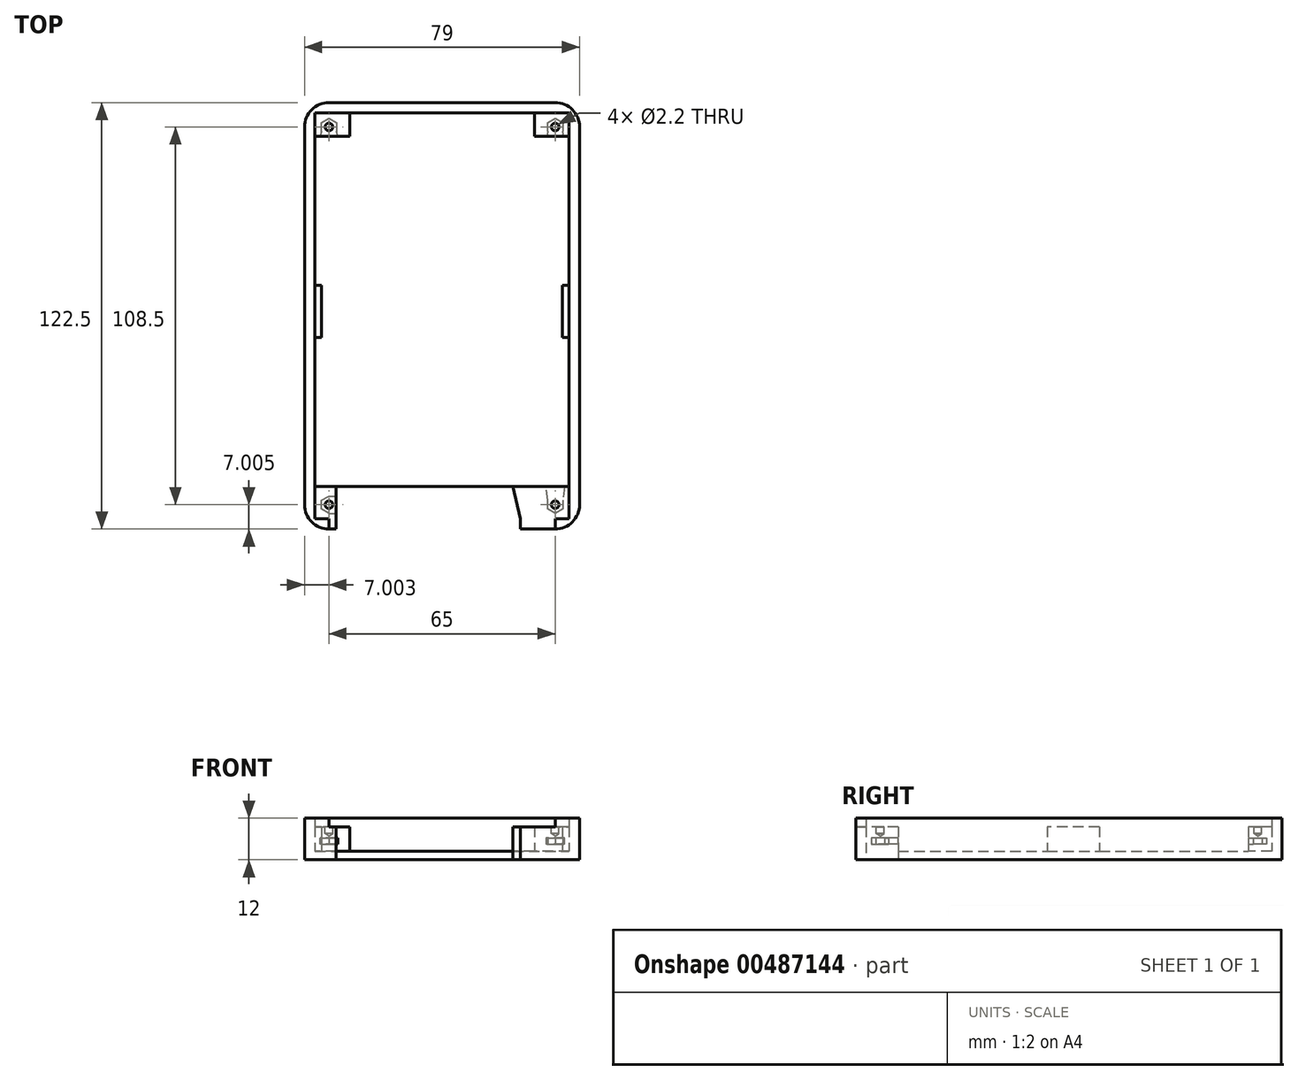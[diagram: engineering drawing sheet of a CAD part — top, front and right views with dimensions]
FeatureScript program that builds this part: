
annotation { "Feature Type Name" : "Feature", "Feature Type Description" : "" }
export const myFeature = defineFeature(function(context is Context, id is Id, definition is map)
    precondition{}
    {
        {
            var Q0;
            Q0=qCreatedBy(makeId("Top.planeOp"),FACE);
            var sketch = newSketch(context, id + "F0", { "sketchPlane" : qUnion([Q0])});
            skLineSegment(sketch, "E0.bottom", {"start": v(-32.56, 61.92) * mm, "end": v(32.44, 61.92) * mm});
            skLineSegment(sketch, "E0.top", {"start": v(-32.56, -60.58) * mm, "end": v(32.44, -60.58) * mm});
            skLineSegment(sketch, "E0.left", {"start": v(-39.56, 54.92) * mm, "end": v(-39.56, -53.58) * mm});
            skLineSegment(sketch, "E0.right", {"start": v(39.44, 54.92) * mm, "end": v(39.44, -53.58) * mm});
            skPoint(sketch, "E1.visualSharp", {"position": v(-39.56, 61.92) * mm});
            skArc(sketch, "E1.filletArc", {"start": v(-32.56, 61.92) * mm, "mid": v(-37.5, 59.87) * mm, "end": v(-39.56, 54.92) * mm});
            skPoint(sketch, "E2.visualSharp", {"position": v(39.44, 61.92) * mm});
            skArc(sketch, "E2.filletArc", {"start": v(39.44, 54.92) * mm, "mid": v(37.4, 59.87) * mm, "end": v(32.44, 61.92) * mm});
            skPoint(sketch, "E3.visualSharp", {"position": v(-39.56, -60.58) * mm});
            skArc(sketch, "E3.filletArc", {"start": v(-39.56, -53.58) * mm, "mid": v(-37.5, -58.53) * mm, "end": v(-32.56, -60.58) * mm});
            skPoint(sketch, "E4.visualSharp", {"position": v(39.44, -60.58) * mm});
            skArc(sketch, "E4.filletArc", {"start": v(32.44, -60.58) * mm, "mid": v(37.4, -58.53) * mm, "end": v(39.44, -53.58) * mm});
            skLineSegment(sketch, "E5.bottom", {"start": v(-32.56, 58.92) * mm, "end": v(32.44, 58.92) * mm});
            skLineSegment(sketch, "E5.top", {"start": v(-32.56, -57.58) * mm, "end": v(32.44, -57.58) * mm});
            skLineSegment(sketch, "E5.left", {"start": v(-36.56, 54.92) * mm, "end": v(-36.56, -53.58) * mm});
            skLineSegment(sketch, "E5.right", {"start": v(36.44, 54.92) * mm, "end": v(36.44, -53.58) * mm});
            skPoint(sketch, "E6.visualSharp", {"position": v(-36.56, 58.92) * mm});
            skArc(sketch, "E6.filletArc", {"start": v(-32.56, 58.92) * mm, "mid": v(-35.39, 57.75) * mm, "end": v(-36.56, 54.92) * mm});
            skPoint(sketch, "E7.visualSharp", {"position": v(36.44, 58.92) * mm});
            skArc(sketch, "E7.filletArc", {"start": v(36.44, 54.92) * mm, "mid": v(35.27, 57.75) * mm, "end": v(32.44, 58.92) * mm});
            skPoint(sketch, "E8.visualSharp", {"position": v(-36.56, -57.58) * mm});
            skArc(sketch, "E8.filletArc", {"start": v(-36.56, -53.58) * mm, "mid": v(-35.39, -56.4) * mm, "end": v(-32.56, -57.58) * mm});
            skPoint(sketch, "E9.visualSharp", {"position": v(36.44, -57.58) * mm});
            skArc(sketch, "E9.filletArc", {"start": v(32.44, -57.58) * mm, "mid": v(35.27, -56.4) * mm, "end": v(36.44, -53.58) * mm});
            skSolve(sketch);
        }
        {
            var Q0;
            Q0=qCreatedBy(makeId("Top.planeOp"),FACE);
            var sketch = newSketch(context, id + "F1", { "sketchPlane" : qUnion([Q0])});
            skLineSegment(sketch, "E10.bottom", {"start": v(-34.66, 51.92) * mm, "end": v(34.54, 51.92) * mm});
            skLineSegment(sketch, "E10.top", {"start": v(-34.66, -48.08) * mm, "end": v(34.54, -48.08) * mm});
            skLineSegment(sketch, "E10.left", {"start": v(-34.66, 51.92) * mm, "end": v(-34.66, -48.08) * mm});
            skLineSegment(sketch, "E10.right", {"start": v(34.54, 51.92) * mm, "end": v(34.54, -48.08) * mm});
            skSolve(sketch);
        }
        {
            var Q0;
            Q0=qCreatedBy(makeId("Top.planeOp"),FACE);
            var sketch = newSketch(context, id + "F2", { "sketchPlane" : qUnion([Q0])});
            skLineSegment(sketch, "E11.bottom", {"start": v(-34.66, 9.42) * mm, "end": v(-36.56, 9.42) * mm});
            skLineSegment(sketch, "E11.top", {"start": v(-34.66, -5.58) * mm, "end": v(-36.56, -5.58) * mm});
            skLineSegment(sketch, "E11.left", {"start": v(-34.66, 9.42) * mm, "end": v(-34.66, -5.58) * mm});
            skLineSegment(sketch, "E11.right", {"start": v(-36.56, 9.42) * mm, "end": v(-36.56, -5.58) * mm});
            skLineSegment(sketch, "E12.bottom", {"start": v(36.44, 9.42) * mm, "end": v(34.54, 9.42) * mm});
            skLineSegment(sketch, "E12.top", {"start": v(36.44, -5.58) * mm, "end": v(34.54, -5.58) * mm});
            skLineSegment(sketch, "E12.left", {"start": v(36.44, 9.42) * mm, "end": v(36.44, -5.58) * mm});
            skLineSegment(sketch, "E12.right", {"start": v(34.54, 9.42) * mm, "end": v(34.54, -5.58) * mm});
            skLineSegment(sketch, "E13.bottom", {"start": v(-36.56, -48.38) * mm, "end": v(-30.46, -48.38) * mm});
            skLineSegment(sketch, "E13.top", {"start": v(-36.56, -57.58) * mm, "end": v(-30.46, -57.58) * mm});
            skLineSegment(sketch, "E13.left", {"start": v(-36.56, -48.38) * mm, "end": v(-36.56, -57.58) * mm});
            skLineSegment(sketch, "E13.right", {"start": v(-30.46, -48.38) * mm, "end": v(-30.46, -57.58) * mm});
            skLineSegment(sketch, "E14.bottom", {"start": v(36.44, -48.38) * mm, "end": v(20.34, -48.38) * mm});
            skLineSegment(sketch, "E14.top", {"start": v(36.44, -57.58) * mm, "end": v(22.44, -57.58) * mm});
            skLineSegment(sketch, "E14.left", {"start": v(36.44, -48.38) * mm, "end": v(36.44, -57.58) * mm});
            skLineSegment(sketch, "E14.right", {"start": v(20.34, -48.38) * mm, "end": v(20.34, -48.38) * mm});
            skLineSegment(sketch, "E15", {"start": v(20.34, -48.38) * mm, "end": v(22.44, -57.58) * mm});
            skLineSegment(sketch, "E16.bottom", {"start": v(-26.56, 58.92) * mm, "end": v(-36.56, 58.92) * mm});
            skLineSegment(sketch, "E16.top", {"start": v(-26.56, 52.22) * mm, "end": v(-36.56, 52.22) * mm});
            skLineSegment(sketch, "E16.left", {"start": v(-26.56, 58.92) * mm, "end": v(-26.56, 52.22) * mm});
            skLineSegment(sketch, "E16.right", {"start": v(-36.56, 58.92) * mm, "end": v(-36.56, 52.22) * mm});
            skLineSegment(sketch, "E17.bottom", {"start": v(26.44, 52.22) * mm, "end": v(36.44, 52.22) * mm});
            skLineSegment(sketch, "E17.top", {"start": v(36.44, 58.92) * mm, "end": v(26.44, 58.92) * mm});
            skLineSegment(sketch, "E17.left", {"start": v(36.44, 52.22) * mm, "end": v(36.44, 58.92) * mm});
            skLineSegment(sketch, "E17.right", {"start": v(26.44, 52.22) * mm, "end": v(26.44, 58.92) * mm});
            skSolve(sketch);
        }
        {
            var Q0;
            Q0=qCreatedBy(makeId("Top.planeOp"),FACE);
            var sketch = newSketch(context, id + "F3", { "sketchPlane" : qUnion([Q0])});
            skCircle(sketch, "E18.cCircle", {"center": v(-32.56, -53.58) * mm, "radius": 2.48 * mm, "construction": true});
            skLineSegment(sketch, "E18.0", {"start": v(-30.4, -54.82) * mm, "end": v(-32.56, -56.06) * mm});
            skLineSegment(sketch, "E18.1", {"start": v(-32.56, -56.06) * mm, "end": v(-34.7, -54.82) * mm});
            skLineSegment(sketch, "E18.2", {"start": v(-34.7, -54.82) * mm, "end": v(-34.7, -52.33) * mm});
            skLineSegment(sketch, "E18.3", {"start": v(-34.7, -52.33) * mm, "end": v(-32.56, -51.1) * mm});
            skLineSegment(sketch, "E18.4", {"start": v(-32.56, -51.1) * mm, "end": v(-30.4, -52.33) * mm});
            skLineSegment(sketch, "E18.5", {"start": v(-30.4, -52.33) * mm, "end": v(-30.4, -54.82) * mm});
            skLineSegment(sketch, "E19.bottom", {"start": v(-32.56, -51.1) * mm, "end": v(-30.46, -51.1) * mm});
            skLineSegment(sketch, "E19.top", {"start": v(-32.56, -56.06) * mm, "end": v(-30.46, -56.06) * mm});
            skLineSegment(sketch, "E19.left", {"start": v(-32.56, -51.1) * mm, "end": v(-32.56, -56.06) * mm});
            skLineSegment(sketch, "E19.right", {"start": v(-30.46, -51.1) * mm, "end": v(-30.46, -56.06) * mm});
            skCircle(sketch, "E20.cCircle", {"center": v(32.44, -53.58) * mm, "radius": 2.48 * mm, "construction": true});
            skLineSegment(sketch, "E20.0", {"start": v(34.6, -52.33) * mm, "end": v(34.6, -54.82) * mm});
            skLineSegment(sketch, "E20.1", {"start": v(34.6, -54.82) * mm, "end": v(32.44, -56.06) * mm});
            skLineSegment(sketch, "E20.2", {"start": v(32.44, -56.06) * mm, "end": v(30.3, -54.82) * mm});
            skLineSegment(sketch, "E20.3", {"start": v(30.3, -54.82) * mm, "end": v(30.3, -52.33) * mm});
            skLineSegment(sketch, "E20.4", {"start": v(30.3, -52.33) * mm, "end": v(32.44, -51.1) * mm});
            skLineSegment(sketch, "E20.5", {"start": v(32.44, -51.1) * mm, "end": v(34.6, -52.33) * mm});
            skCircle(sketch, "E21.cCircle", {"center": v(32.44, 54.92) * mm, "radius": 2.48 * mm, "construction": true});
            skLineSegment(sketch, "E21.0", {"start": v(34.6, 53.68) * mm, "end": v(32.44, 52.44) * mm});
            skLineSegment(sketch, "E21.1", {"start": v(32.44, 52.44) * mm, "end": v(30.3, 53.68) * mm});
            skLineSegment(sketch, "E21.2", {"start": v(30.3, 53.68) * mm, "end": v(30.3, 56.17) * mm});
            skLineSegment(sketch, "E21.3", {"start": v(30.3, 56.17) * mm, "end": v(32.44, 57.4) * mm});
            skLineSegment(sketch, "E21.4", {"start": v(32.44, 57.4) * mm, "end": v(34.6, 56.17) * mm});
            skLineSegment(sketch, "E21.5", {"start": v(34.6, 56.17) * mm, "end": v(34.6, 53.68) * mm});
            skLineSegment(sketch, "E22", {"start": v(30.3, -52.33) * mm, "end": v(29.68, -47.75) * mm});
            skLineSegment(sketch, "E23", {"start": v(29.68, -47.75) * mm, "end": v(35.2, -47.75) * mm});
            skLineSegment(sketch, "E24", {"start": v(35.2, -47.75) * mm, "end": v(34.6, -52.33) * mm});
            skLineSegment(sketch, "E25", {"start": v(30.3, 53.68) * mm, "end": v(29.86, 51.36) * mm});
            skLineSegment(sketch, "E26", {"start": v(29.86, 51.36) * mm, "end": v(35.15, 51.36) * mm});
            skLineSegment(sketch, "E27", {"start": v(35.15, 51.36) * mm, "end": v(34.6, 53.68) * mm});
            skCircle(sketch, "E28.cCircle", {"center": v(-32.56, 54.92) * mm, "radius": 2.48 * mm, "construction": true});
            skLineSegment(sketch, "E28.0", {"start": v(-32.56, 52.44) * mm, "end": v(-34.7, 53.68) * mm});
            skLineSegment(sketch, "E28.1", {"start": v(-34.7, 53.68) * mm, "end": v(-34.7, 56.17) * mm});
            skLineSegment(sketch, "E28.2", {"start": v(-34.7, 56.17) * mm, "end": v(-32.56, 57.4) * mm});
            skLineSegment(sketch, "E28.3", {"start": v(-32.56, 57.4) * mm, "end": v(-30.4, 56.17) * mm});
            skLineSegment(sketch, "E28.4", {"start": v(-30.4, 56.17) * mm, "end": v(-30.4, 53.68) * mm});
            skLineSegment(sketch, "E28.5", {"start": v(-30.4, 53.68) * mm, "end": v(-32.56, 52.44) * mm});
            skLineSegment(sketch, "E29", {"start": v(-34.7, 53.68) * mm, "end": v(-35.33, 51.36) * mm});
            skLineSegment(sketch, "E30", {"start": v(-35.33, 51.36) * mm, "end": v(-29.8, 51.36) * mm});
            skLineSegment(sketch, "E31", {"start": v(-29.8, 51.36) * mm, "end": v(-30.4, 53.68) * mm});
            skSolve(sketch);
        }
        {
            var Q0;
            Q0=makeQuery(id+"F0.imprint","IMPRINT",FACE,{"disambiguationData":[TD([[makeQuery(id+"F0.imprint","IMPRINT",EDGE,{"derivedFrom":sQuery(id+"F0.wireOp",EDGE,"E0.bottom")}),-1.0]])]});
            var Q1;
            Q1=makeQuery(id+"F0.imprint","IMPRINT",FACE,{"disambiguationData":[TD([[makeQuery(id+"F0.imprint","IMPRINT",EDGE,{"derivedFrom":sQuery(id+"F0.wireOp",EDGE,"E5.bottom")}),-1.0]])]});
            extrude(context, id + "F4", {"entities" : qUnion([Q0, Q1]), "depth" : 2.4 * mm});
        }
        {
            var Q0;
            Q0=makeQuery(id+"F0.imprint","IMPRINT",FACE,{"disambiguationData":[TD([[makeQuery(id+"F0.imprint","IMPRINT",EDGE,{"derivedFrom":sQuery(id+"F0.wireOp",EDGE,"E0.bottom")}),-1.0]])]});
            extrude(context, id + "F5", {"entities" : qUnion([Q0]), "operationType" : NewBodyOperationType.ADD, "depth" : 12 * mm});
        }
        {
            var Q0;
            Q0 = qSketchRegion(id + "F2", true);
            extrude(context, id + "F6", {"entities" : qUnion([Q0]), "operationType" : NewBodyOperationType.ADD, "depth" : 12 * mm});
        }
        {
            var Q0;
            Q0=qCreatedBy(makeId("Top.planeOp"),FACE);
            cPlane(context, id + "F7", {"entities" : qUnion([Q0]), "cplaneType" : CPlaneType.OFFSET, "offset" : 20 * mm, "width" : 150 * mm, "height" : 150 * mm});
        }
        {
            var Q0;
            Q0=qCreatedBy(id+"F7.planeOp",FACE);
            var sketch = newSketch(context, id + "F8", { "sketchPlane" : qUnion([Q0])});
            skPoint(sketch, "E32", {"position": v(-32.56, 54.92) * mm});
            skPoint(sketch, "E33", {"position": v(32.44, 54.92) * mm});
            skPoint(sketch, "E34", {"position": v(-32.56, -53.58) * mm});
            skPoint(sketch, "E35", {"position": v(32.44, -53.58) * mm});
            skSolve(sketch);
        }
        {
            var Q0;
            Q0 = qSketchRegion(id + "F2", true);
            extrude(context, id + "F9", {"entities" : qUnion([Q0]), "operationType" : NewBodyOperationType.REMOVE, "depth" : 12 * mm, "hasSecondDirection" : true, "secondDirectionOppositeDirection" : false, "secondDirectionDepth" : 9.5 * mm});
        }
        {
            var Q0;
            Q0=qCreatedBy(makeId("Front.planeOp"),FACE);
            cPlane(context, id + "F10", {"entities" : qUnion([Q0]), "cplaneType" : CPlaneType.OFFSET, "offset" : 57.58 * mm, "width" : 150 * mm, "height" : 150 * mm});
        }
        {
            var Q0;
            Q0=qCreatedBy(id+"F10.planeOp",FACE);
            var sketch = newSketch(context, id + "F11", { "sketchPlane" : qUnion([Q0])});
            skLineSegment(sketch, "E36.bottom", {"start": v(-30.46, 12) * mm, "end": v(22.44, 12) * mm});
            skLineSegment(sketch, "E36.top", {"start": v(-30.46, 0) * mm, "end": v(22.44, 0) * mm});
            skLineSegment(sketch, "E36.left", {"start": v(-30.46, 12) * mm, "end": v(-30.46, 0) * mm});
            skLineSegment(sketch, "E36.right", {"start": v(22.44, 12) * mm, "end": v(22.44, 0) * mm});
            skSolve(sketch);
        }
        {
            var Q0;
            Q0=qCreatedBy(id+"F10.planeOp",FACE);
            var sketch = newSketch(context, id + "F12", { "sketchPlane" : qUnion([Q0])});
            skLineSegment(sketch, "E37.bottom", {"start": v(-32.56, 12) * mm, "end": v(32.44, 12) * mm});
            skLineSegment(sketch, "E37.top", {"start": v(-32.56, 9.5) * mm, "end": v(32.44, 9.5) * mm});
            skLineSegment(sketch, "E37.left", {"start": v(-32.56, 12) * mm, "end": v(-32.56, 9.5) * mm});
            skLineSegment(sketch, "E37.right", {"start": v(32.44, 12) * mm, "end": v(32.44, 9.5) * mm});
            skSolve(sketch);
        }
        {
            var Q0;
            Q0 = qSketchRegion(id + "F11", true);
            extrude(context, id + "F13", {"entities" : qUnion([Q0]), "operationType" : NewBodyOperationType.REMOVE, "depth" : 9.9 * mm, "hasSecondDirection" : true, "secondDirectionOppositeDirection" : true, "secondDirectionDepth" : 9.2 * mm});
        }
        {
            var Q0;
            Q0 = qSketchRegion(id + "F12", true);
            extrude(context, id + "F14", {"entities" : qUnion([Q0]), "operationType" : NewBodyOperationType.REMOVE, "depth" : 25 * mm});
        }
        {
            var Q0;
            Q0=makeQuery(id+"F2.imprint","IMPRINT",FACE,{"disambiguationData":[TD([[makeQuery(id+"F2.imprint","IMPRINT",EDGE,{"derivedFrom":sQuery(id+"F2.wireOp",EDGE,"E14.bottom")}),1.0]])]});
            extrude(context, id + "F15", {"entities" : qUnion([Q0]), "operationType" : NewBodyOperationType.ADD, "depth" : 9.5 * mm});
        }
        {
            var Q0;
            Q0=sQuery(id+"F8.wireOp",VERTEX,"E32");
            var Q1;
            Q1=sQuery(id+"F8.wireOp",VERTEX,"E34");
            var Q2;
            Q2=sQuery(id+"F8.wireOp",VERTEX,"E35");
            var Q3;
            Q3=sQuery(id+"F8.wireOp",VERTEX,"E33");
            var Q4;
            Q4=makeQuery(id+"F4.opExtrude","SWEPT_BODY",BODY,{"disambiguationData":[OSD([sQuery(id+"F0.wireOp",EDGE,"E0.bottom"),sQuery(id+"F0.wireOp",EDGE,"E0.top"),sQuery(id+"F0.wireOp",EDGE,"E0.left"),sQuery(id+"F0.wireOp",EDGE,"E0.right"),sQuery(id+"F0.wireOp",EDGE,"E1.filletArc"),sQuery(id+"F0.wireOp",EDGE,"E2.filletArc"),sQuery(id+"F0.wireOp",EDGE,"E3.filletArc"),sQuery(id+"F0.wireOp",EDGE,"E4.filletArc")])]});
            hole(context, id + "F16", {"style" : HoleStyle.SIMPLE, "endStyle" : HoleEndStyle.BLIND, "holeDiameter" : 2.2 * mm, "holeDepth" : 2 * mm, "isTappedThrough" : true, "tappedDepth" : 12 * mm, "tapClearance" : 3, "locations" : qUnion([Q0, Q1, Q2, Q3]), "scope" : qUnion([Q4])});
        }
        {
            var Q0;
            Q0 = qSketchRegion(id + "F3", true);
            extrude(context, id + "F17", {"entities" : qUnion([Q0]), "operationType" : NewBodyOperationType.REMOVE, "depth" : 6.3 * mm, "hasSecondDirection" : true, "secondDirectionOppositeDirection" : false, "secondDirectionDepth" : 4.5 * mm});
        }
    });
